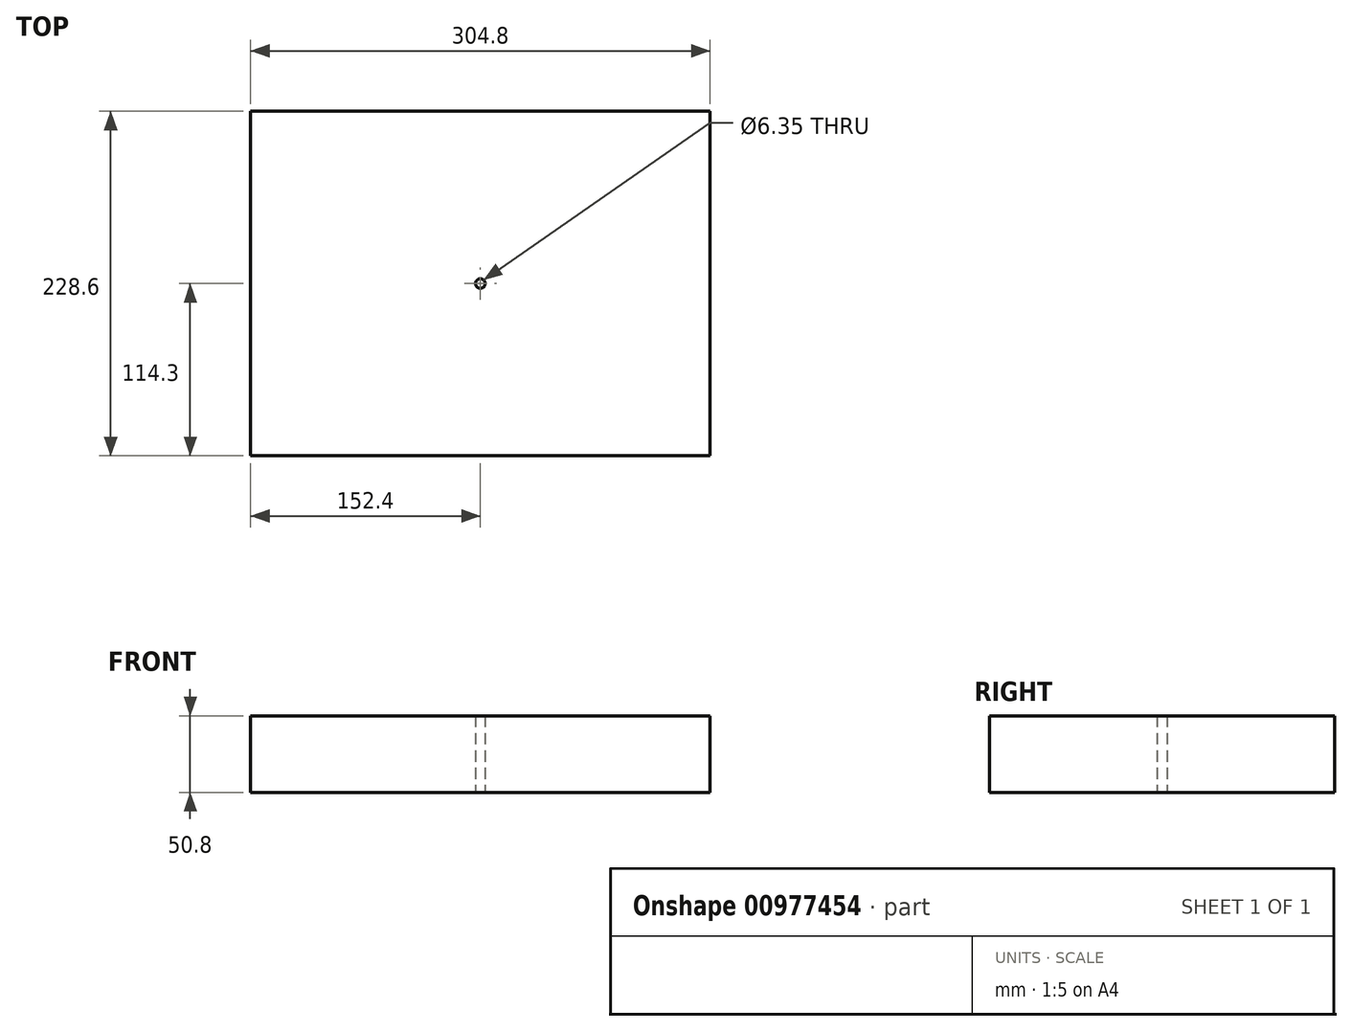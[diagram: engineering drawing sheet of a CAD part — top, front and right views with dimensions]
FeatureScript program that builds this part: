
annotation { "Feature Type Name" : "Feature", "Feature Type Description" : "" }
export const myFeature = defineFeature(function(context is Context, id is Id, definition is map)
    precondition{}
    {
        {
            var Q0;
            Q0=qCreatedBy(makeId("Top.planeOp"),FACE);
            var sketch = newSketch(context, id + "F0", { "sketchPlane" : qUnion([Q0])});
            skLineSegment(sketch, "E0.bottom", {"start": v(152.4, 114.3) * mm, "end": v(-152.4, 114.3) * mm});
            skLineSegment(sketch, "E0.top", {"start": v(152.4, -114.3) * mm, "end": v(-152.4, -114.3) * mm});
            skLineSegment(sketch, "E0.left", {"start": v(152.4, 114.3) * mm, "end": v(152.4, -114.3) * mm});
            skLineSegment(sketch, "E0.right", {"start": v(-152.4, 114.3) * mm, "end": v(-152.4, -114.3) * mm});
            skPoint(sketch, "E0.middle", {"position": v(0, 0) * mm});
            skCircle(sketch, "E1", {"center": v(0, 0) * mm, "radius": 3.18 * mm});
            skSolve(sketch);
        }
        {
            var Q0;
            Q0 = qSketchRegion(id + "F0", true);
            extrude(context, id + "F1", {"entities" : qUnion([Q0]), "depth" : 50.8 * mm, "offsetDistance" : 25.4 * mm});
        }
    });
